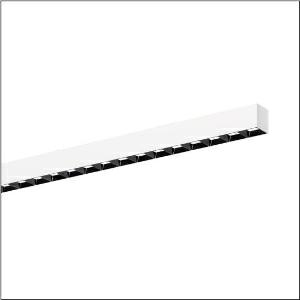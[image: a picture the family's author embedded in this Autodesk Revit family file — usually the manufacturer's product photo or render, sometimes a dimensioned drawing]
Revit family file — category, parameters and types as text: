
# Revit family: silica_r__21_51mx22dc4awb_3425
name_source: partatom
category: Lighting Fixtures
units: mm (PartAtom-declared; Revit-internal decimal feet)

## family parameters
Cut with Voids When Loaded = No
Host = Face
Light Source = No
Part Type = Normal
Room Calculation Point = No
Round Connector Dimension = Use Diameter
Shared = No

## types (1)
- --- (1 x LED, 10800 lm, 64.7 W, 4000K)
    Apparent Load = 65 VA
    CIE Flux Codes = 86 100 100 100 100
    Color Rendering = 80
    Color Temperature = 4000K
    Default Elevation = 1800 mm
    Description = Silica® 21, office luminaire, primary light control with darklight reflector, of PMMA, black, CAT 2 (L<= 3000cd/m²), light emission: direct distribution, primary light characteristic: symmetric, installation type: surface-mounted, LED, rated luminous flux: 10.800lm, luminous efficacy: 167lm/W, light colour: 840, colour temperature: 4000K, with terminal, 3+2-pole, max. 2.5mm², mains connection: 220..240V, AC, 50/60Hz, rated input power: 64.7W, luminaire housing, of aluminium, traffic white (RAL 9016), length: 3.004mm, width: 53mm, height: 53mm, protection rating (complete): IP20, insulation class (complete): insulation class I (protective earthing), certification: CE, permissible operating ambient temperature: 0..+35°C, standard: EN 50419, packaging unit: 1 piece
    Height = 0 mm  [stored 0 ft]
    Lamp = 1 x LED
    Lamp Light Flux = 10800 lm
    Lamp Power = 64.7 W
    Lamp count = 1
    Length = 3004 mm
    Luminous efficacy = 167 lm/W
    Manufacturer = Siteco
    ModVariant = No
    Model = 51MX22DC4AWB
    Mounting Place = Ceiling
    Mounting Type = Recessed
    Number of Poles = 1
    OnlyDefault = Yes
    Power Factor = 1
    Product Name = Silica® 21
    Product group = office luminaire | ceiling recessed
    ProductGroupID = 401
    Protection Class = Protection class I
    Protection Degree = IP 20
    RLX_Detail_Level = 1
    RLX_Emergency_Light_Flux = 0 lm
    RLX_Emergency_Type = 0
    RLX_Emergency_Type_DB = No
    RlxData = <blob elided: 62241 chars, md5=c2922282>
    Socket = socket
    Standby Power = 0 W
    System Light Flux = 10800 lm
    System Power = 65 W
    Type Comments = factory setting: luminous flux: 100 % | dim-lin: 254 | 366 mA
    Type Image = l_1313592.jpg
    URL = http://relux.com
    VarID = @adj_074491
    Voltage = 0 V
    Weight = 0.00 kg
    Width = 53 mm

note: [stored X ft] marks values corroborated as IEEE doubles in the binary element streams (Revit-internal decimal feet)

## geometry (parser evidence)
native form markers: Blend x4, Sweep x11
no freeform markers — native parametric forms only
